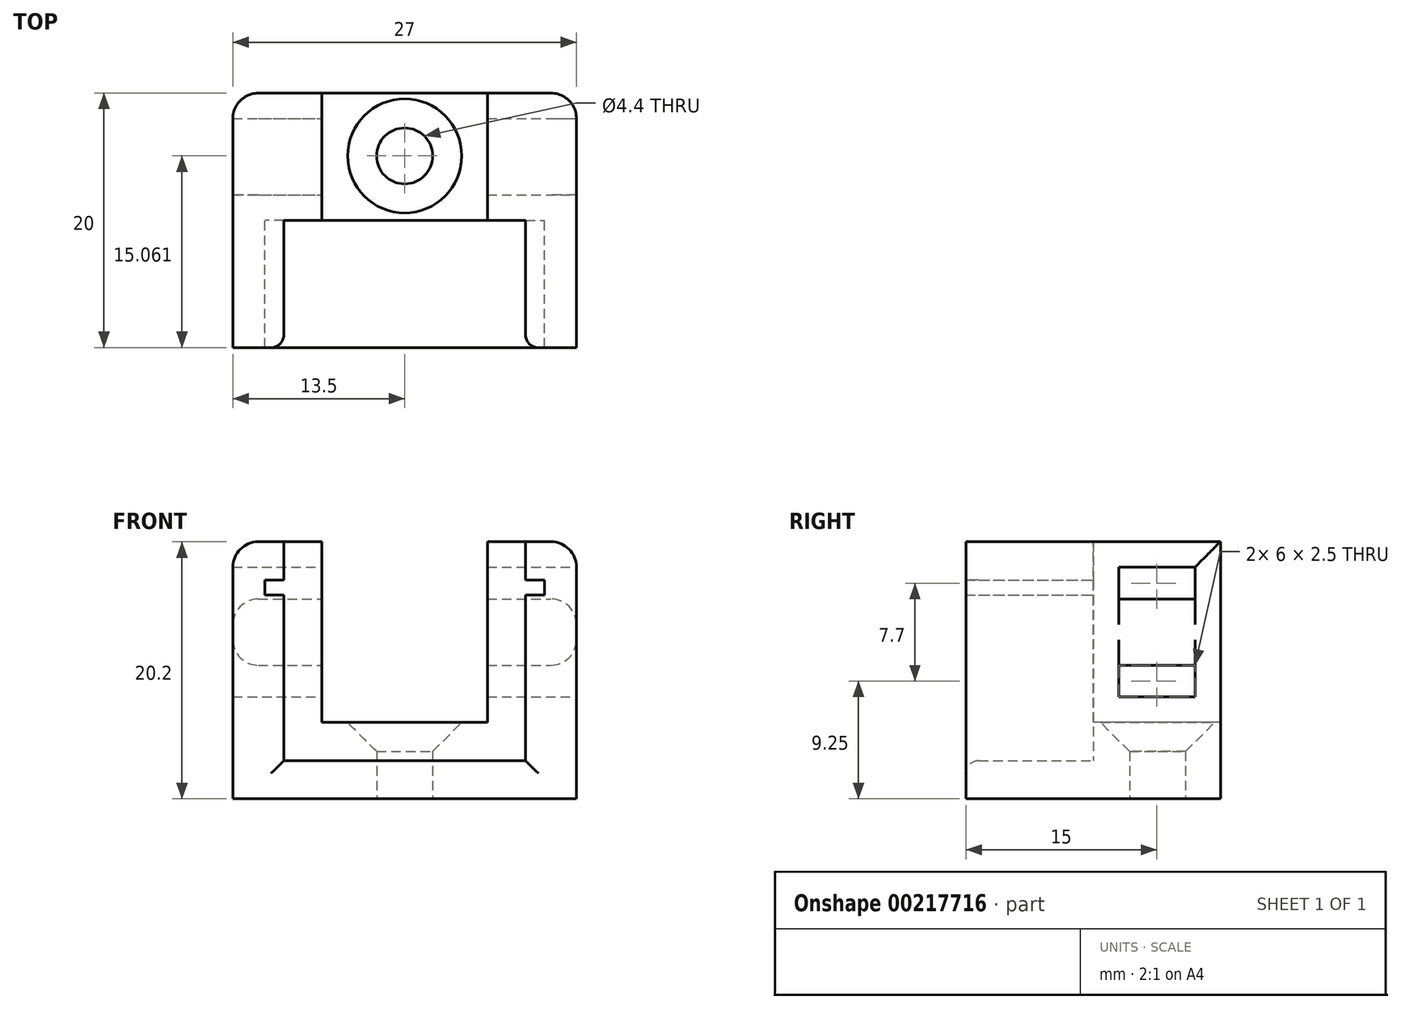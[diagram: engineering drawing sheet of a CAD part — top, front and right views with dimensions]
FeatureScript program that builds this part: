
annotation { "Feature Type Name" : "Feature", "Feature Type Description" : "" }
export const myFeature = defineFeature(function(context is Context, id is Id, definition is map)
    precondition{}
    {
        {
            var Q0;
            Q0=qCreatedBy(makeId("Front.planeOp"),FACE);
            var sketch = newSketch(context, id + "F0", { "sketchPlane" : qUnion([Q0])});
            skLineSegment(sketch, "E0", {"start": v(-13.5, 0) * mm, "end": v(13.5, 0) * mm});
            skLineSegment(sketch, "E1", {"start": v(13.5, 0) * mm, "end": v(13.5, 20.2) * mm});
            skLineSegment(sketch, "E2", {"start": v(13.5, 20.2) * mm, "end": v(9.5, 20.2) * mm});
            skLineSegment(sketch, "E3", {"start": v(9.5, 20.2) * mm, "end": v(9.5, 17.2) * mm});
            skLineSegment(sketch, "E4", {"start": v(9.5, 17.2) * mm, "end": v(11, 17.2) * mm});
            skLineSegment(sketch, "E5", {"start": v(11, 17.2) * mm, "end": v(11, 16) * mm});
            skLineSegment(sketch, "E6", {"start": v(11, 16) * mm, "end": v(9.5, 16) * mm});
            skLineSegment(sketch, "E7", {"start": v(9.5, 16) * mm, "end": v(9.5, 3) * mm});
            skLineSegment(sketch, "E8", {"start": v(9.5, 3) * mm, "end": v(-9.5, 3) * mm});
            skLineSegment(sketch, "E9", {"start": v(-9.5, 3) * mm, "end": v(-9.5, 16) * mm});
            skLineSegment(sketch, "E10", {"start": v(-9.5, 16) * mm, "end": v(-11, 16) * mm});
            skLineSegment(sketch, "E11", {"start": v(-11, 16) * mm, "end": v(-11, 17.2) * mm});
            skLineSegment(sketch, "E12", {"start": v(-11, 17.2) * mm, "end": v(-9.5, 17.2) * mm});
            skLineSegment(sketch, "E13", {"start": v(-9.5, 17.2) * mm, "end": v(-9.5, 20.2) * mm});
            skLineSegment(sketch, "E14", {"start": v(-9.5, 20.2) * mm, "end": v(-13.5, 20.2) * mm});
            skLineSegment(sketch, "E15", {"start": v(-13.5, 20.2) * mm, "end": v(-13.5, 0) * mm});
            skLineSegment(sketch, "E16", {"start": v(0, 0) * mm, "end": v(0, 29.5) * mm, "construction": true});
            skSolve(sketch);
        }
        {
            var Q0;
            Q0=makeQuery(id+"F0.imprint","IMPRINT",FACE,{"disambiguationData":[TD([[makeQuery(id+"F0.imprint","IMPRINT",EDGE,{"derivedFrom":sQuery(id+"F0.wireOp",EDGE,"E0")}),1.0]])]});
            extrude(context, id + "F1", {"entities" : qUnion([Q0]), "depth" : 10 * mm});
        }
        {
            var Q0;
            Q0=qCreatedBy(makeId("Front.planeOp"),FACE);
            var sketch = newSketch(context, id + "F2", { "sketchPlane" : qUnion([Q0])});
            skLineSegment(sketch, "E17.0", {"start": v(13.5, 0) * mm, "end": v(13.5, 20.2) * mm});
            skLineSegment(sketch, "E17.1", {"start": v(-13.5, 0) * mm, "end": v(13.5, 0) * mm});
            skLineSegment(sketch, "E17.2", {"start": v(-13.5, 20.2) * mm, "end": v(-13.5, 0) * mm});
            skLineSegment(sketch, "E18.0", {"start": v(9.5, 3) * mm, "end": v(-9.5, 3) * mm, "construction": true});
            skLineSegment(sketch, "E19", {"start": v(13.5, 20.2) * mm, "end": v(-13.5, 20.2) * mm});
            skLineSegment(sketch, "E20.0", {"start": v(9.5, 6) * mm, "end": v(-9.5, 6) * mm});
            skLineSegment(sketch, "E21", {"start": v(9.5, 6) * mm, "end": v(9.5, 20.2) * mm, "construction": true});
            skLineSegment(sketch, "E22", {"start": v(-9.5, 6) * mm, "end": v(-9.5, 20.2) * mm, "construction": true});
            skLineSegment(sketch, "E23.0", {"start": v(-6.5, 6) * mm, "end": v(-6.5, 20.2) * mm});
            skLineSegment(sketch, "E24.0", {"start": v(6.5, 6) * mm, "end": v(6.5, 20.2) * mm});
            skSolve(sketch);
        }
        {
            var Q0;
            Q0=makeQuery(id+"F2.imprint","IMPRINT",FACE,{"disambiguationData":[TD([[makeQuery(id+"F2.imprint","IMPRINT",EDGE,{"derivedFrom":sQuery(id+"F2.wireOp",EDGE,"E17.0")}),1.0]])]});
            extrude(context, id + "F3", {"entities" : qUnion([Q0]), "operationType" : NewBodyOperationType.ADD, "oppositeDirection" : true, "depth" : 10 * mm});
        }
        {
            var Q0;
            Q0=makeQuery(id+"F3.opExtrude","SWEPT_FACE",FACE,{"disambiguationData":[OSD([sQuery(id+"F2.wireOp",EDGE,"E20.0")])]});
            var sketch = newSketch(context, id + "F4", { "sketchPlane" : qUnion([Q0])});
            skPoint(sketch, "E25", {"position": v(0, 5.06) * mm});
            skSolve(sketch);
        }
        {
            var Q0;
            Q0=sQuery(id+"F4.wireOp",VERTEX,"E25");
            var Q1;
            Q1=makeQuery(id+"F1.opExtrude","SWEPT_BODY",BODY,{"disambiguationData":[OSD([sQuery(id+"F0.wireOp",EDGE,"E0"),sQuery(id+"F0.wireOp",EDGE,"E1"),sQuery(id+"F0.wireOp",EDGE,"E2"),sQuery(id+"F0.wireOp",EDGE,"E3"),sQuery(id+"F0.wireOp",EDGE,"E4"),sQuery(id+"F0.wireOp",EDGE,"E5"),sQuery(id+"F0.wireOp",EDGE,"E6"),sQuery(id+"F0.wireOp",EDGE,"E7"),sQuery(id+"F0.wireOp",EDGE,"E8"),sQuery(id+"F0.wireOp",EDGE,"E9"),sQuery(id+"F0.wireOp",EDGE,"E10"),sQuery(id+"F0.wireOp",EDGE,"E11"),sQuery(id+"F0.wireOp",EDGE,"E12"),sQuery(id+"F0.wireOp",EDGE,"E13"),sQuery(id+"F0.wireOp",EDGE,"E14"),sQuery(id+"F0.wireOp",EDGE,"E15")])]});
            hole(context, id + "F5", {"style" : HoleStyle.C_SINK, "endStyle" : HoleEndStyle.THROUGH, "standardTappedOrClearance" : lookupTablePath({ "standard" : "ISO", "fit" : "Normal", "size" : "M4", "type" : "Clearance" }), "standardBlindInLast" : lookupTablePath({ "fit" : "Standard", "standard" : "ISO", "size" : "M4", "type" : "Clearance" }), "holeDiameter" : 4.4 * mm, "cSinkDiameter" : 8.96 * mm, "cSinkAngle" : 90 * degree, "locations" : qUnion([Q0]), "scope" : qUnion([Q1]), "isTappedThrough" : true, "startStyle" : HoleStartStyle.PART});
        }
        {
            var Q0;
            Q0=makeQuery(id+"F1.opExtrude","CAP_EDGE",EDGE,{"disambiguationData":[OSD([sQuery(id+"F0.wireOp",EDGE,"E8")])],"isStart":false});
            var Q1;
            Q1=makeQuery(id+"F1.opExtrude","CAP_EDGE",EDGE,{"disambiguationData":[OSD([sQuery(id+"F0.wireOp",EDGE,"E9")])],"isStart":false});
            var Q2;
            Q2=makeQuery(id+"F1.opExtrude","CAP_EDGE",EDGE,{"disambiguationData":[OSD([sQuery(id+"F0.wireOp",EDGE,"E13")])],"isStart":false});
            var Q3;
            Q3=makeQuery(id+"F1.opExtrude","CAP_EDGE",EDGE,{"disambiguationData":[OSD([sQuery(id+"F0.wireOp",EDGE,"E3")])],"isStart":false});
            var Q4;
            Q4=makeQuery(id+"F1.opExtrude","CAP_EDGE",EDGE,{"disambiguationData":[OSD([sQuery(id+"F0.wireOp",EDGE,"E7")])],"isStart":false});
            fillet(context, id + "F6", {"entities" : qUnion([Q0, Q1, Q2, Q3, Q4]), "radius" : 1 * mm, "tangentPropagation" : true, "allowEdgeOverflow" : false});
        }
        {
            var Q0;
            Q0=makeQuery(id+"F3.boolean.opBoolean","MERGE",EDGE,{"derivedFrom":[makeQuery(id+"F1.opExtrude","SWEPT_EDGE",EDGE,{"disambiguationData":[OSD([sQuery(id+"F0.wireOp",EDGE,"E14"),sQuery(id+"F0.wireOp",EDGE,"E15")])]}),makeQuery(id+"F3.opExtrude","SWEPT_EDGE",EDGE,{"disambiguationData":[OSD([sQuery(id+"F2.wireOp",EDGE,"E17.2"),sQuery(id+"F2.wireOp",EDGE,"E19")])]})]});
            var Q1;
            Q1=makeQuery(id+"F3.opExtrude","CAP_EDGE",EDGE,{"disambiguationData":[OSD([sQuery(id+"F2.wireOp",EDGE,"E17.2")])],"isStart":false});
            var Q2;
            Q2=makeQuery(id+"F3.opExtrude","CAP_EDGE",EDGE,{"disambiguationData":[OSD([sQuery(id+"F2.wireOp",EDGE,"E17.0")])],"isStart":false});
            var Q3;
            Q3=makeQuery(id+"F3.boolean.opBoolean","MERGE",EDGE,{"derivedFrom":[makeQuery(id+"F1.opExtrude","SWEPT_EDGE",EDGE,{"disambiguationData":[OSD([sQuery(id+"F0.wireOp",EDGE,"E1"),sQuery(id+"F0.wireOp",EDGE,"E2")])]}),makeQuery(id+"F3.opExtrude","SWEPT_EDGE",EDGE,{"disambiguationData":[OSD([sQuery(id+"F2.wireOp",EDGE,"E17.0"),sQuery(id+"F2.wireOp",EDGE,"E19")])]})]});
            fillet(context, id + "F7", {"entities" : qUnion([Q0, Q1, Q2, Q3]), "radius" : 2 * mm, "tangentPropagation" : true, "allowEdgeOverflow" : false});
        }
        {
            var Q0;
            Q0=makeQuery(id+"F3.opExtrude","SWEPT_FACE",FACE,{"disambiguationData":[OSD([sQuery(id+"F2.wireOp",EDGE,"E23.0")])]});
            var sketch = newSketch(context, id + "F8", { "sketchPlane" : qUnion([Q0])});
            skLineSegment(sketch, "E26.0", {"start": v(2, 8) * mm, "end": v(2, 18.2) * mm, "construction": true});
            skLineSegment(sketch, "E26.1", {"start": v(8, 8) * mm, "end": v(2, 8) * mm});
            skLineSegment(sketch, "E26.2", {"start": v(8, 8) * mm, "end": v(8, 18.2) * mm, "construction": true});
            skLineSegment(sketch, "E26.3", {"start": v(8, 18.2) * mm, "end": v(2, 18.2) * mm});
            skLineSegment(sketch, "E27", {"start": v(2, 18.2) * mm, "end": v(2, 15.7) * mm});
            skLineSegment(sketch, "E28", {"start": v(2, 15.7) * mm, "end": v(8, 15.7) * mm});
            skLineSegment(sketch, "E29", {"start": v(8, 15.7) * mm, "end": v(8, 18.2) * mm});
            skLineSegment(sketch, "E30", {"start": v(2, 8) * mm, "end": v(2, 10.5) * mm});
            skLineSegment(sketch, "E31", {"start": v(2, 10.5) * mm, "end": v(8, 10.5) * mm});
            skLineSegment(sketch, "E32", {"start": v(8, 10.5) * mm, "end": v(8, 8) * mm});
            skSolve(sketch);
        }
        {
            var Q0;
            Q0=makeQuery(id+"F8.imprint","IMPRINT",FACE,{"disambiguationData":[TD([[makeQuery(id+"F8.imprint","IMPRINT",EDGE,{"derivedFrom":sQuery(id+"F8.wireOp",EDGE,"E26.3")}),1.0]])]});
            var Q1;
            Q1=makeQuery(id+"F8.imprint","IMPRINT",FACE,{"disambiguationData":[TD([[makeQuery(id+"F8.imprint","IMPRINT",EDGE,{"derivedFrom":sQuery(id+"F8.wireOp",EDGE,"E26.1")}),-1.0]])]});
            extrude(context, id + "F9", {"entities" : qUnion([Q0, Q1]), "operationType" : NewBodyOperationType.REMOVE, "endBound" : BoundingType.THROUGH_ALL, "oppositeDirection" : true, "depth" : 25 * mm, "hasSecondDirection" : true, "secondDirectionBound" : BoundingType.THROUGH_ALL, "secondDirectionOppositeDirection" : false, "secondDirectionDepth" : 25 * mm});
        }
        {
            var Q0;
            Q0=makeQuery(id+"F9.boolean.opBoolean","INTERSECT",EDGE,{"derivedFrom":[makeQuery(id+"F3.boolean.opBoolean","MERGE",FACE,{"derivedFrom":[makeQuery(id+"F1.opExtrude","SWEPT_FACE",FACE,{"disambiguationData":[OSD([sQuery(id+"F0.wireOp",EDGE,"E15")])]}),makeQuery(id+"F3.opExtrude","SWEPT_FACE",FACE,{"disambiguationData":[OSD([sQuery(id+"F2.wireOp",EDGE,"E17.2")])]})]}),makeQuery(id+"F9.opExtrude","SWEPT_FACE",FACE,{"disambiguationData":[OSD([sQuery(id+"F8.wireOp",EDGE,"E28")])]})]});
            var Q1;
            Q1=makeQuery(id+"F9.boolean.opBoolean","INTERSECT",EDGE,{"derivedFrom":[makeQuery(id+"F3.boolean.opBoolean","MERGE",FACE,{"derivedFrom":[makeQuery(id+"F1.opExtrude","SWEPT_FACE",FACE,{"disambiguationData":[OSD([sQuery(id+"F0.wireOp",EDGE,"E15")])]}),makeQuery(id+"F3.opExtrude","SWEPT_FACE",FACE,{"disambiguationData":[OSD([sQuery(id+"F2.wireOp",EDGE,"E17.2")])]})]}),makeQuery(id+"F9.opExtrude","SWEPT_FACE",FACE,{"disambiguationData":[OSD([sQuery(id+"F8.wireOp",EDGE,"E31")])]})]});
            var Q2;
            Q2=makeQuery(id+"F9.boolean.opBoolean","INTERSECT",EDGE,{"derivedFrom":[makeQuery(id+"F3.boolean.opBoolean","MERGE",FACE,{"derivedFrom":[makeQuery(id+"F1.opExtrude","SWEPT_FACE",FACE,{"disambiguationData":[OSD([sQuery(id+"F0.wireOp",EDGE,"E1")])]}),makeQuery(id+"F3.opExtrude","SWEPT_FACE",FACE,{"disambiguationData":[OSD([sQuery(id+"F2.wireOp",EDGE,"E17.0")])]})]}),makeQuery(id+"F9.opExtrude","SWEPT_FACE",FACE,{"disambiguationData":[OSD([sQuery(id+"F8.wireOp",EDGE,"E28")])]})]});
            var Q3;
            Q3=makeQuery(id+"F9.boolean.opBoolean","INTERSECT",EDGE,{"derivedFrom":[makeQuery(id+"F3.boolean.opBoolean","MERGE",FACE,{"derivedFrom":[makeQuery(id+"F1.opExtrude","SWEPT_FACE",FACE,{"disambiguationData":[OSD([sQuery(id+"F0.wireOp",EDGE,"E1")])]}),makeQuery(id+"F3.opExtrude","SWEPT_FACE",FACE,{"disambiguationData":[OSD([sQuery(id+"F2.wireOp",EDGE,"E17.0")])]})]}),makeQuery(id+"F9.opExtrude","SWEPT_FACE",FACE,{"disambiguationData":[OSD([sQuery(id+"F8.wireOp",EDGE,"E31")])]})]});
            fillet(context, id + "F10", {"entities" : qUnion([Q0, Q1, Q2, Q3]), "radius" : 2 * mm, "tangentPropagation" : true, "allowEdgeOverflow" : false});
        }
    });
